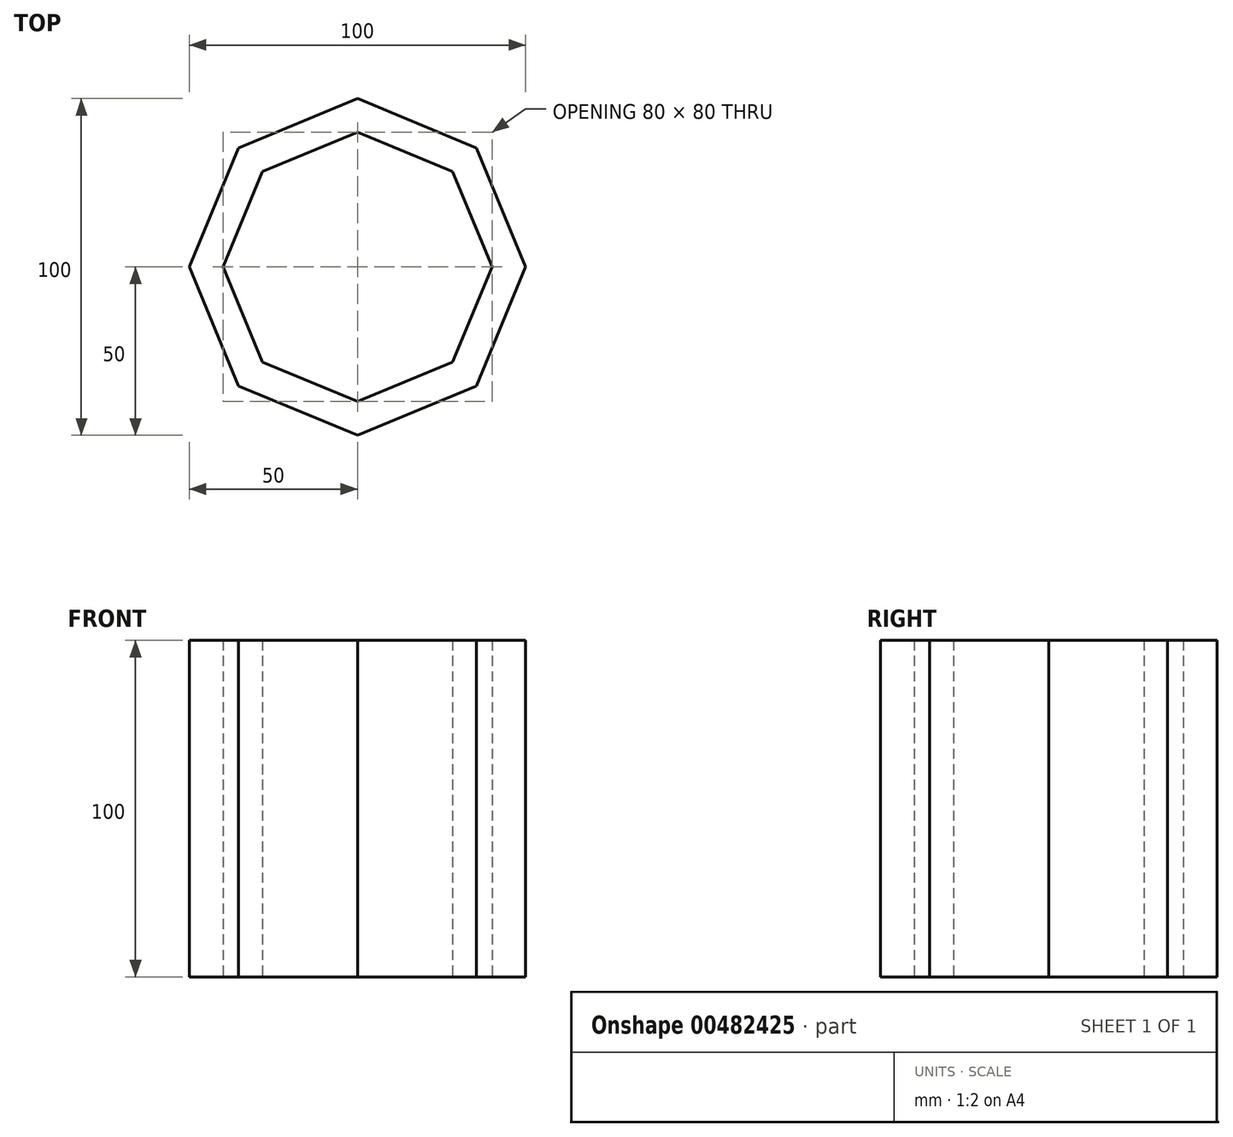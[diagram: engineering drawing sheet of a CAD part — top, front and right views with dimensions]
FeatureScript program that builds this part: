
annotation { "Feature Type Name" : "Feature", "Feature Type Description" : "" }
export const myFeature = defineFeature(function(context is Context, id is Id, definition is map)
    precondition{}
    {
        {
            var Q0;
            Q0=qCreatedBy(makeId("Top.planeOp"),FACE);
            var sketch = newSketch(context, id + "F0", { "sketchPlane" : qUnion([Q0])});
            skCircle(sketch, "E0.cCircle", {"center": v(0, 0) * mm, "radius": 46.2 * mm, "construction": true});
            skLineSegment(sketch, "E0.0", {"start": v(0, 50) * mm, "end": v(35.36, 35.36) * mm});
            skLineSegment(sketch, "E0.1", {"start": v(35.36, 35.36) * mm, "end": v(50, 0) * mm});
            skLineSegment(sketch, "E0.2", {"start": v(50, 0) * mm, "end": v(35.36, -35.36) * mm});
            skLineSegment(sketch, "E0.3", {"start": v(35.36, -35.36) * mm, "end": v(0, -50) * mm});
            skLineSegment(sketch, "E0.4", {"start": v(0, -50) * mm, "end": v(-35.36, -35.36) * mm});
            skLineSegment(sketch, "E0.5", {"start": v(-35.36, -35.36) * mm, "end": v(-50, 0) * mm});
            skLineSegment(sketch, "E0.6", {"start": v(-50, 0) * mm, "end": v(-35.36, 35.36) * mm});
            skLineSegment(sketch, "E0.7", {"start": v(-35.36, 35.36) * mm, "end": v(0, 50) * mm});
            skPoint(sketch, "E0.0.midPoint", {"position": v(17.68, 42.68) * mm});
            skSolve(sketch);
        }
        {
            var Q0;
            Q0=makeQuery(id+"F0.imprint","IMPRINT",FACE,{"disambiguationData":[TD([[makeQuery(id+"F0.imprint","IMPRINT",EDGE,{"derivedFrom":sQuery(id+"F0.wireOp",EDGE,"E0.0")}),-1.0]])]});
            extrude(context, id + "F1", {"entities" : qUnion([Q0]), "depth" : 100 * mm});
        }
        {
            var Q0;
            Q0=qCreatedBy(makeId("Top.planeOp"),FACE);
            var sketch = newSketch(context, id + "F2", { "sketchPlane" : qUnion([Q0])});
            skCircle(sketch, "E1.cCircle", {"center": v(0, 0) * mm, "radius": 36.96 * mm, "construction": true});
            skLineSegment(sketch, "E1.0", {"start": v(-28.28, -28.28) * mm, "end": v(-40, 0) * mm});
            skLineSegment(sketch, "E1.1", {"start": v(-40, 0) * mm, "end": v(-28.28, 28.28) * mm});
            skLineSegment(sketch, "E1.2", {"start": v(-28.28, 28.28) * mm, "end": v(0, 40) * mm});
            skLineSegment(sketch, "E1.3", {"start": v(0, 40) * mm, "end": v(28.28, 28.28) * mm});
            skLineSegment(sketch, "E1.4", {"start": v(28.28, 28.28) * mm, "end": v(40, 0) * mm});
            skLineSegment(sketch, "E1.5", {"start": v(40, 0) * mm, "end": v(28.28, -28.28) * mm});
            skLineSegment(sketch, "E1.6", {"start": v(28.28, -28.28) * mm, "end": v(0, -40) * mm});
            skLineSegment(sketch, "E1.7", {"start": v(0, -40) * mm, "end": v(-28.28, -28.28) * mm});
            skPoint(sketch, "E1.0.midPoint", {"position": v(-34.14, -14.14) * mm});
            skSolve(sketch);
        }
        {
            var Q0;
            Q0=makeQuery(id+"F2.imprint","IMPRINT",FACE,{"disambiguationData":[TD([[makeQuery(id+"F2.imprint","IMPRINT",EDGE,{"derivedFrom":sQuery(id+"F2.wireOp",EDGE,"E1.0")}),-1.0]])]});
            extrude(context, id + "F3", {"entities" : qUnion([Q0]), "operationType" : NewBodyOperationType.REMOVE, "depth" : 105.4 * mm});
        }
    });
